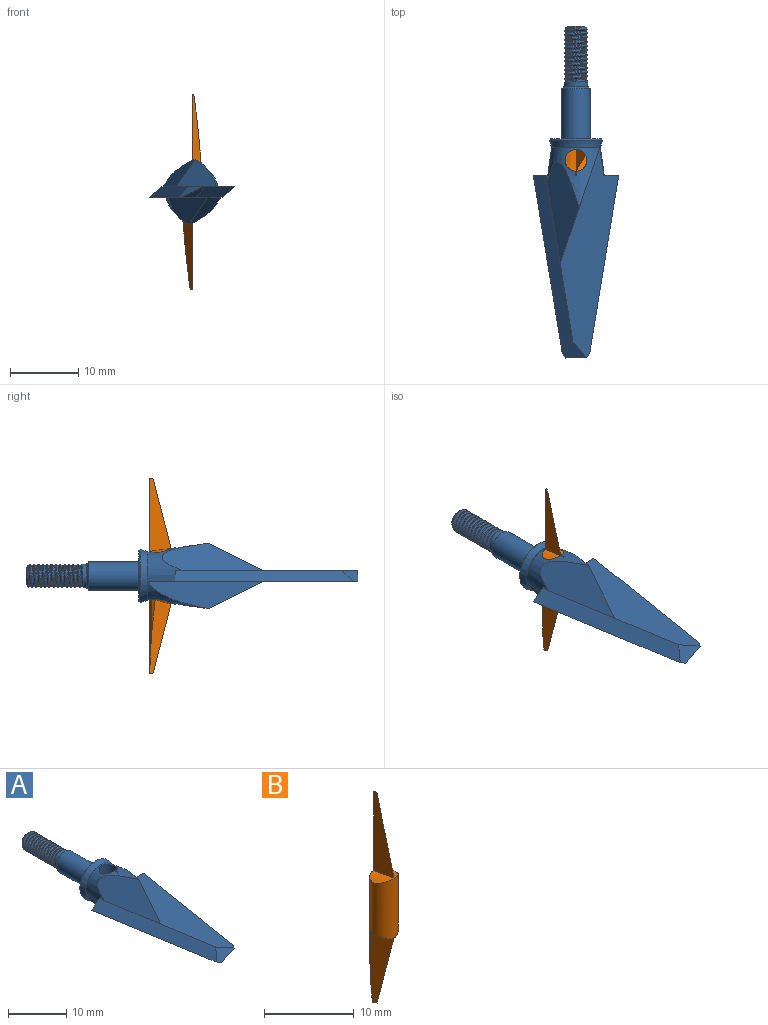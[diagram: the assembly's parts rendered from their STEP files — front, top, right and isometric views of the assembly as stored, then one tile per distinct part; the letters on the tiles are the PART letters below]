
ASSEMBLY  parts=2 mates=1
PART A: 51 faces, bbox 12.5x285.9x9.6 mm
  f0: cylinder r=2.08mm len=7.37mm, axis (0,-1,0), area 96.4mm2, adj f2,f38
  f1: plane 3.66x3.66mm, normal (0,1,0), area 0.9mm2, adj f2,f3
  f2: cone r=1.83mm half-angle=45deg, axis (0,-1,0), area 4.4mm2, adj f0,f1
  f3: cylinder r=1.75mm len=3.51mm, axis (0,-1,0), area 7.4mm2, adj f1,f4,f18,f19,f21
  f4: cylinder r=1.75mm len=3.51mm, axis (0,-1,0), area 1mm2, adj f3,f5,f19,f21
  f5: cylinder r=1.75mm len=3.51mm, axis (0,-1,0), area 1mm2, adj f4,f6,f19,f21
  f6: cylinder r=1.75mm len=3.51mm, axis (0,-1,0), area 1mm2, adj f5,f7,f19,f21
  f7: cylinder r=1.75mm len=3.51mm, axis (0,-1,0), area 1mm2, adj f6,f8,f19,f21
  f8: cylinder r=1.75mm len=3.51mm, axis (0,-1,0), area 1mm2, adj f7,f9,f19,f21
  f9: cylinder r=1.75mm len=3.51mm, axis (0,-1,0), area 1mm2, adj f8,f10,f19,f21
  f10: cylinder r=1.75mm len=3.51mm, axis (0,-1,0), area 1mm2, adj f9,f11,f19,f21
  f11: cylinder r=1.75mm len=3.51mm, axis (0,-1,0), area 1mm2, adj f10,f12,f19,f21
  f12: cylinder r=1.75mm len=3.51mm, axis (0,-1,0), area 1mm2, adj f11,f13,f19,f21
  f13: cylinder r=1.75mm len=3.51mm, axis (0,-1,0), area 1mm2, adj f12,f14,f19,f21
  f14: cylinder r=1.75mm len=3.51mm, axis (0,-1,0), area 1mm2, adj f13,f15,f19,f21
  f15: cylinder r=1.75mm len=1.33mm, axis (0,-1,0), area 0.1mm2, adj f14,f17,f21
  f16: plane 2.49x2.49mm, normal (0,1,0), area 4.9mm2, adj f17
  f17: cone r=1.24mm half-angle=45deg, axis (0,-1,0), area 4.6mm2, adj f15,f16,f19,f20,f21
  f18: plane 0.55x0.27mm, normal (0,0,-1), area 0.1mm2, adj f3,f19,f20,f21
  f19: bspline ~8.47x4.05mm, area 45.1mm2, adj f3,f4,f5,f6,f7,f8,f9,f10
  f20: cylinder r=1.48mm len=8.16mm, axis (0,1,0), area 20.7mm2, adj f17,f18,f19,f21
  f21: bspline ~8.23x4.05mm, area 41.3mm2, adj f3,f4,f5,f6,f7,f8,f9,f10
  f22: cone r=3.56mm half-angle=8deg, axis (0,-1,0), area 35.5mm2, adj f24,f25,f26,f27,f28,f29,f39,f41
  f23: plane 0.05x0.04mm, normal (0,-1,0), area 0mm2, adj f25,f26,f30
  f24: plane 0.17x0.15mm, normal (0,1,0), area 0mm2, adj f22,f41,f42
  f25: plane 16.76x5.76mm, normal (0.95,-0.33,0), area 42.1mm2, adj f22,f23,f26,f30
  f26: plane 14.64x4.66mm, normal (-0.7,-0.11,0.71), area 52.8mm2, adj f22,f23,f25,f36
  f27: plane 1.13x0.34mm, normal (0,0,1), area 0.2mm2, adj f22,f28,f36
  f28: plane 2.18x1.52mm, normal (0,1,0), area 1.9mm2, adj f22,f27,f29,f36
  f29: plane 30.73x8.58mm, normal (0,0,-1), area 128.7mm2, adj f22,f28,f32,f34,f35,f36,f45,f47
  f30: plane 30.74x8.58mm, normal (0,0,1), area 128.7mm2, adj f23,f25,f31,f32,f34,f35,f36,f44
  f31: plane 2.18x1.52mm, normal (0,1,0), area 1.9mm2, adj f30,f33,f35,f44
  f32: plane 3.52x2.44mm, normal (-0.42,-0.34,0.84), area 5.5mm2, adj f29,f30,f34,f36
  f33: plane 1.13x0.34mm, normal (0,0,-1), area 0.2mm2, adj f31,f35,f44
  f34: plane 3.52x2.44mm, normal (0.42,-0.34,-0.84), area 5.5mm2, adj f29,f30,f32,f35
  f35: plane 26.09x5.78mm, normal (0.63,-0.1,-0.77), area 60.4mm2, adj f29,f30,f31,f33,f34,f48
  f36: plane 26.09x5.78mm, normal (-0.63,-0.1,0.77), area 60.4mm2, adj f26,f27,f28,f29,f30,f32
  f37: cone r=3.94mm half-angle=16deg, axis (0,1,0), area 27mm2, adj f39,f40
  f38: plane 7.54x7.54mm, normal (0,1,0), area 31mm2, adj f0,f40
  f39: plane 7.15x7.15mm, normal (0,-1,0), area 0.4mm2, adj f22,f37,f44
  f40: torus R=3.77mm, axis (0,1,0), area 5.7mm2, adj f37,f38
  f41: bspline ~259.18x0.4mm, area 0.1mm2, adj f22,f24,f42,f43
  f42: bspline ~259.18x0.38mm, area 0.1mm2, adj f22,f24,f41,f43
  f43: cylinder r=1.59mm len=8.08mm, axis (0,0,-1), area 72.7mm2, adj f22,f41,f42,f44,f49,f50
  f44: cone r=3.56mm half-angle=8deg, axis (0,-1,0), area 35.5mm2, adj f30,f31,f33,f39,f43,f46,f47,f48
  f45: plane 0.05x0.05mm, normal (0,-1,0), area 0mm2, adj f29,f47,f48
  f46: plane 0.17x0.15mm, normal (0,1,0), area 0mm2, adj f44,f49,f50
  f47: plane 16.76x5.76mm, normal (-0.95,-0.32,0), area 42.2mm2, adj f29,f44,f45,f48
  f48: plane 14.64x4.66mm, normal (0.7,-0.11,-0.71), area 52.9mm2, adj f35,f44,f45,f47
  f49: bspline ~259.18x0.4mm, area 0.1mm2, adj f43,f44,f46,f50
  f50: bspline ~259.18x0.38mm, area 0.1mm2, adj f43,f44,f46,f49
PART B: 11 faces, bbox 3.4x3.2x28.6 mm
  f0: cylinder r=1.59mm len=28.58mm, axis (0,0,-1), area 93.6mm2, adj f1,f2,f3,f4,f5,f6,f7,f8
  f1: plane 0.51x0.27mm, normal (0,0,-1), area 0.1mm2, adj f0,f3,f9
  f2: plane 0.51x0.27mm, normal (0,0,1), area 0.1mm2, adj f0,f4,f7
  f3: plane 10.69x3.18mm, normal (1,0,0), area 19.6mm2, adj f0,f1,f6,f9
  f4: plane 10.69x3.18mm, normal (-1,0,0), area 19.6mm2, adj f0,f2,f5,f7
  f5: cone r=3.56mm half-angle=8deg, axis (0,-1,0), area 4.1mm2, adj f0,f4
  f6: cone r=3.56mm half-angle=8deg, axis (0,-1,0), area 4.1mm2, adj f0,f3
  f7: plane 10.85x3.15mm, normal (0.87,-0.48,0.13), area 18.9mm2, adj f0,f2,f4,f8
  f8: cone r=3.56mm half-angle=8deg, axis (0,-1,0), area 1.6mm2, adj f0,f7
  f9: plane 10.85x3.15mm, normal (-0.87,-0.48,-0.13), area 18.9mm2, adj f0,f1,f3,f10
  f10: cone r=3.56mm half-angle=8deg, axis (0,-1,0), area 1.6mm2, adj f0,f9
PLACE A at identity fixed
PLACE B t=(0,4.06,0)mm
MATE cylindrical A.f43 <-> B.f0  axis (0,0,-1) through (0,2.21,0)mm
